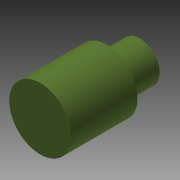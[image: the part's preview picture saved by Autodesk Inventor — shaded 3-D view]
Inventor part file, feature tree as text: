
AUTODESK INVENTOR PART (.ipt)
format: ipt  version: 2014 (Build 180170000, 170)  size: 81,920 bytes
history: native  units: mm
features: extrude x2, sketch x2, other x1
ambient origin geometry x8: Origin, YZ Plane, XZ Plane, XY Plane, X Axis, Y Axis, Z Axis, Center Point
bodies: Body1 (feature_tree)
feature tree (5):
  other  "Твердое тело1"
  extrude  "Выдавливание1"  Depth=5.6mm
  extrude  "Выдавливание2"  Depth=6.0mm TaperAngle=0.0deg
  sketch  "Эскиз1"
  sketch  "Эскиз2"
